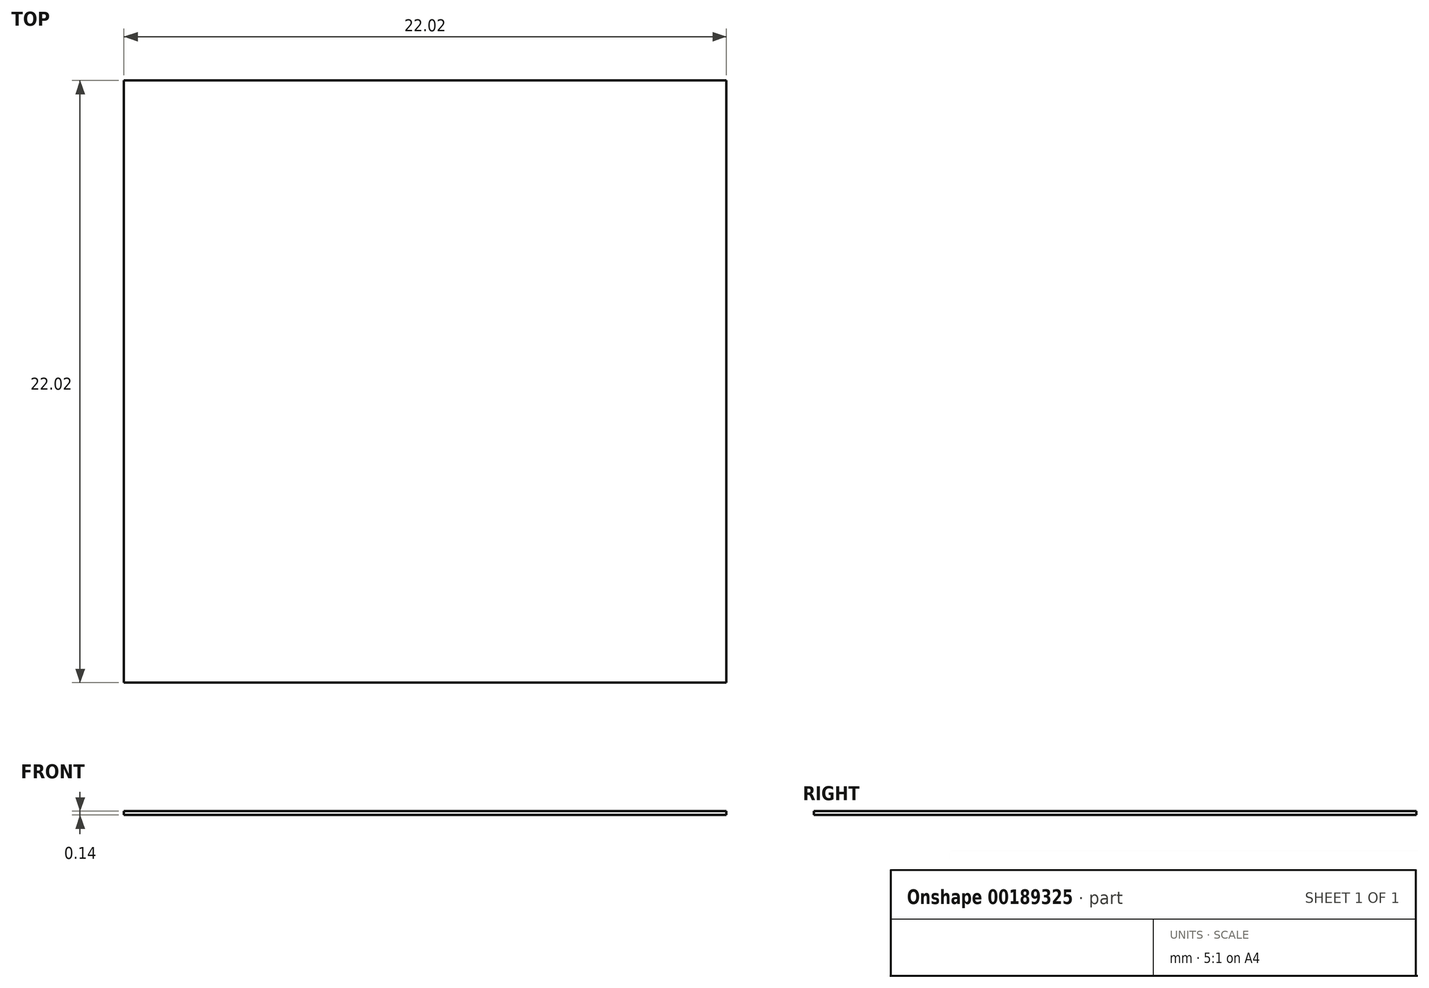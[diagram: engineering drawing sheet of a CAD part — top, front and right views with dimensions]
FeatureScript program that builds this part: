
annotation { "Feature Type Name" : "Feature", "Feature Type Description" : "" }
export const myFeature = defineFeature(function(context is Context, id is Id, definition is map)
    precondition{}
    {
        {
            var Q0;
            Q0=qCreatedBy(makeId("Top.planeOp"),FACE);
            var sketch = newSketch(context, id + "F0", { "sketchPlane" : qUnion([Q0])});
            skLineSegment(sketch, "E0.bottom", {"start": v(11.01, 11.01) * mm, "end": v(-11.01, 11.01) * mm});
            skLineSegment(sketch, "E0.top", {"start": v(11.01, -11.01) * mm, "end": v(-11.01, -11.01) * mm});
            skLineSegment(sketch, "E0.left", {"start": v(11.01, 11.01) * mm, "end": v(11.01, -11.01) * mm});
            skLineSegment(sketch, "E0.right", {"start": v(-11.01, 11.01) * mm, "end": v(-11.01, -11.01) * mm});
            skPoint(sketch, "E0.middle", {"position": v(0, 0) * mm});
            skSolve(sketch);
        }
        {
            var Q0;
            Q0=makeQuery(id+"F0.imprint","IMPRINT",FACE,{"disambiguationData":[TD([[makeQuery(id+"F0.imprint","IMPRINT",EDGE,{"derivedFrom":sQuery(id+"F0.wireOp",EDGE,"E0.bottom")}),1.0]])]});
            extrude(context, id + "F1", {"entities" : qUnion([Q0]), "depth" : 0.14 * mm});
        }
    });
